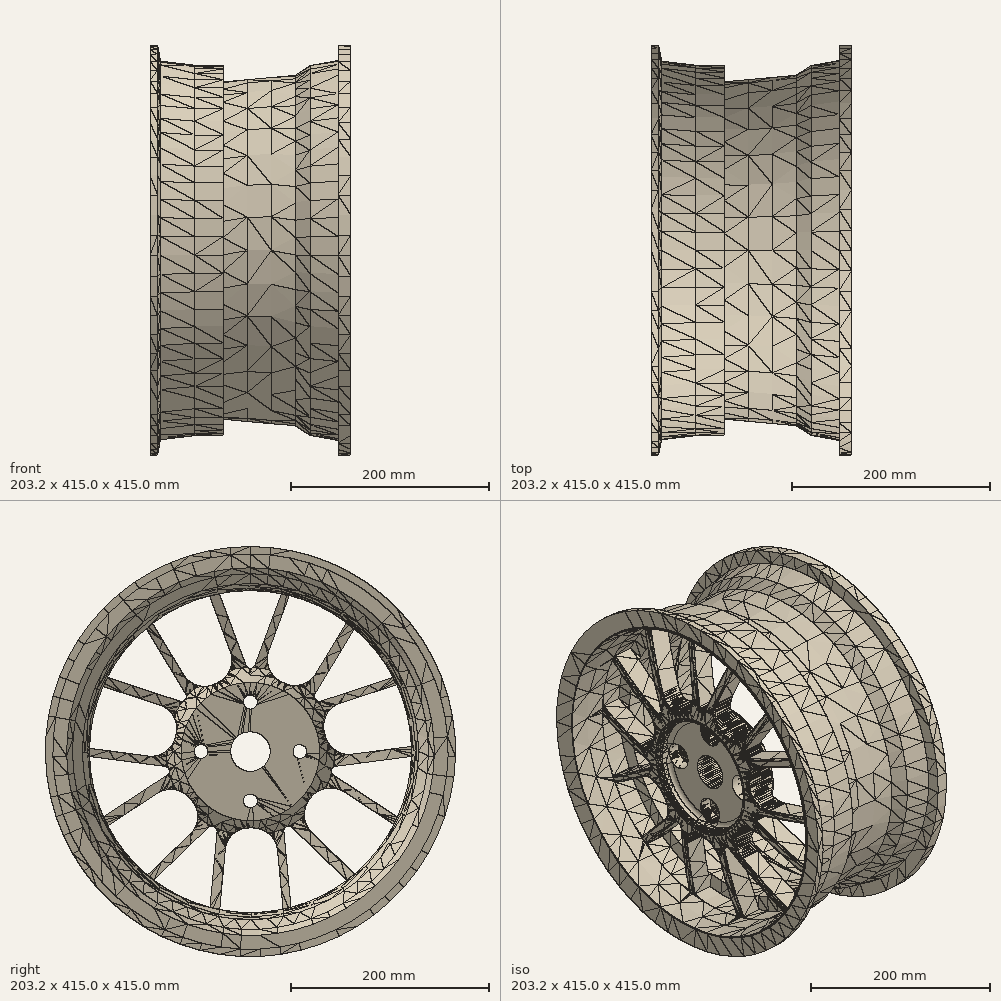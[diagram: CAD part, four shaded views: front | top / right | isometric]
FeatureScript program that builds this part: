
annotation { "Feature Type Name" : "Feature", "Feature Type Description" : "" }
export const myFeature = defineFeature(function(context is Context, id is Id, definition is map)
    precondition{}
    {
        {
            var Q0;
            Q0=qCreatedBy(makeId("Front.planeOp"),FACE);
            var sketch = newSketch(context, id + "F0", { "sketchPlane" : qUnion([Q0])});
            skLineSegment(sketch, "E0", {"start": v(0, 0) * mm, "end": v(203.2, 0) * mm});
            skLineSegment(sketch, "E1", {"start": v(203.2, 0) * mm, "end": v(203.2, 207.5) * mm});
            skPoint(sketch, "E2", {"position": v(203.2, 200) * mm});
            skLineSegment(sketch, "E3", {"start": v(203.2, 200) * mm, "end": v(197.7, 200) * mm});
            skPoint(sketch, "E4", {"position": v(197.7, 186) * mm});
            skLineSegment(sketch, "E5", {"start": v(197.7, 200) * mm, "end": v(197.7, 186) * mm});
            skPoint(sketch, "E6", {"position": v(164.7, 180) * mm});
            skLineSegment(sketch, "E7", {"start": v(164.7, 180) * mm, "end": v(197.7, 186) * mm});
            skPoint(sketch, "E8", {"position": v(149.7, 170) * mm});
            skLineSegment(sketch, "E9", {"start": v(164.7, 180) * mm, "end": v(149.7, 170) * mm});
            skPoint(sketch, "E10", {"position": v(66.7, 162.5) * mm});
            skLineSegment(sketch, "E11", {"start": v(66.7, 162.5) * mm, "end": v(149.7, 170) * mm});
            skLineSegment(sketch, "E12", {"start": v(203.2, 207.5) * mm, "end": v(66.7, 207.5) * mm});
            skLineSegment(sketch, "E13", {"start": v(0, 0) * mm, "end": v(0, 207.5) * mm});
            skPoint(sketch, "E14", {"position": v(2.5, 185) * mm});
            skPoint(sketch, "E15", {"position": v(45, 180) * mm});
            skLineSegment(sketch, "E16", {"start": v(45, 180) * mm, "end": v(66.7, 162.5) * mm});
            skLineSegment(sketch, "E17", {"start": v(2.5, 185) * mm, "end": v(45, 180) * mm});
            skLineSegment(sketch, "E18", {"start": v(0, 207.5) * mm, "end": v(66.7, 207.5) * mm});
            skLineSegment(sketch, "E19", {"start": v(2.5, 185) * mm, "end": v(0, 185) * mm});
            skLineSegment(sketch, "E20", {"start": v(2.5, 185) * mm, "end": v(2.5, 185.9) * mm});
            skLineSegment(sketch, "E21", {"start": v(3.1, 186.5) * mm, "end": v(3.4, 186.5) * mm});
            skLineSegment(sketch, "E22", {"start": v(0, 207.5) * mm, "end": v(4, 186.5) * mm});
            skPoint(sketch, "E23.visualSharp", {"position": v(2.5, 186.5) * mm});
            skArc(sketch, "E23.filletArc", {"start": v(3.1, 186.5) * mm, "mid": v(2.68, 186.32) * mm, "end": v(2.5, 185.9) * mm});
            skLineSegment(sketch, "E24", {"start": v(4, 185.9) * mm, "end": v(4, 185.5) * mm, "construction": true});
            skPoint(sketch, "E25.visualSharp", {"position": v(4, 186.5) * mm});
            skArc(sketch, "E25.filletArc", {"start": v(4, 185.9) * mm, "mid": v(3.82, 186.32) * mm, "end": v(3.4, 186.5) * mm});
            skLineSegment(sketch, "E26", {"start": v(4, 186.5) * mm, "end": v(4, 185.9) * mm});
            skLineSegment(sketch, "E27", {"start": v(66.7, 180) * mm, "end": v(45, 180) * mm});
            skLineSegment(sketch, "E28", {"start": v(66.7, 162.5) * mm, "end": v(66.7, 180) * mm});
            skArc(sketch, "E29", {"start": v(66.7, 162.5) * mm, "mid": v(58.94, 175.08) * mm, "end": v(45, 180) * mm});
            skLineSegment(sketch, "E30.0", {"start": v(203.2, 207.5) * mm, "end": v(190.2, 207.5) * mm});
            skLineSegment(sketch, "E30.1", {"start": v(66.03, 169.97) * mm, "end": v(66.7, 170.03) * mm});
            skLineSegment(sketch, "E30.2", {"start": v(161.83, 187.1) * mm, "end": v(147.13, 177.3) * mm});
            skLineSegment(sketch, "E30.3", {"start": v(161.83, 187.1) * mm, "end": v(190.2, 192.26) * mm});
            skLineSegment(sketch, "E30.4", {"start": v(190.2, 207.5) * mm, "end": v(190.2, 192.26) * mm});
            skLineSegment(sketch, "E31.0", {"start": v(10.67, 191.6) * mm, "end": v(45.44, 187.5) * mm});
            skLineSegment(sketch, "E31.1", {"start": v(7.63, 207.5) * mm, "end": v(10.67, 191.6) * mm});
            skLineSegment(sketch, "E32.0", {"start": v(74.2, 187.5) * mm, "end": v(45.44, 187.5) * mm});
            skLineSegment(sketch, "E32.1", {"start": v(74.2, 162.5) * mm, "end": v(74.2, 163.18) * mm});
            skLineSegment(sketch, "E33.trimOffspring", {"start": v(74.2, 170.7) * mm, "end": v(74.2, 187.5) * mm});
            skLineSegment(sketch, "E34.trimOffspring", {"start": v(74.2, 170.7) * mm, "end": v(147.13, 177.3) * mm});
            skPoint(sketch, "E35", {"position": v(45, -180) * mm});
            skPoint(sketch, "E36", {"position": v(16, 0) * mm});
            skArc(sketch, "E37", {"start": v(45, 180) * mm, "mid": v(23.3, 91.16) * mm, "end": v(16, 0) * mm});
            skArc(sketch, "E38.0", {"start": v(66.7, 162.54) * mm, "mid": v(48.21, 82.2) * mm, "end": v(42, 0) * mm});
            skLineSegment(sketch, "E39", {"start": v(16, 0) * mm, "end": v(42, 0) * mm});
            skLineSegment(sketch, "E40", {"start": v(16, 0) * mm, "end": v(16, 20) * mm});
            skLineSegment(sketch, "E41", {"start": v(16, 20) * mm, "end": v(76, 20) * mm});
            skPoint(sketch, "E42", {"position": v(66.2, 70) * mm});
            skPoint(sketch, "E43", {"position": v(48.64, 85) * mm});
            skLineSegment(sketch, "E44", {"start": v(66.2, 70) * mm, "end": v(48.64, 85) * mm});
            skLineSegment(sketch, "E45", {"start": v(66.2, 70) * mm, "end": v(66.2, 0) * mm});
            skSolve(sketch);
        }
        {
            var Q0;
            {var subQ3=sQuery(id+"F0.wireOp",EDGE,"E38.0");var subQ5=sQuery(id+"F0.wireOp",EDGE,"E41");var subQ7=makeQuery(id+"F0.imprint","INTERSECT",VERTEX,{"derivedFrom":[subQ3,subQ5]});Q0=makeQuery(id+"F0.imprint","IMPRINT",FACE,{"disambiguationData":[TD([[makeQuery(id+"F0.imprint","IMPRINT",EDGE,{"disambiguationData":[TD([[subQ7,1.0]])],"derivedFrom":subQ3}),-1.0]])]});}
            var Q1;
            {var subQ1=sQuery(id+"F0.wireOp",EDGE,"E16");var subQ3=sQuery(id+"F0.wireOp",EDGE,"E38.0");var subQ4=makeQuery(id+"F0.imprint","INTERSECT",VERTEX,{"derivedFrom":[subQ1,subQ3]});Q1=makeQuery(id+"F0.imprint","IMPRINT",FACE,{"disambiguationData":[TD([[makeQuery(id+"F0.imprint","IMPRINT",EDGE,{"disambiguationData":[TD([[subQ4,1.0]])],"derivedFrom":subQ3}),-1.0]])]});}
            var Q2;
            {var subQ1=sQuery(id+"F0.wireOp",EDGE,"E27");Q2=makeQuery(id+"F0.imprint","IMPRINT",FACE,{"disambiguationData":[TD([[makeQuery(id+"F0.imprint","IMPRINT",EDGE,{"derivedFrom":subQ1}),1.0]])]});}
            var Q3;
            {var subQ7=sQuery(id+"F0.wireOp",EDGE,"E3");Q3=makeQuery(id+"F0.imprint","IMPRINT",FACE,{"disambiguationData":[TD([[makeQuery(id+"F0.imprint","IMPRINT",EDGE,{"derivedFrom":subQ7}),-1.0]])]});}
            var Q4;
            {var subQ0=sQuery(id+"F0.wireOp",EDGE,"E44");Q4=makeQuery(id+"F0.imprint","IMPRINT",FACE,{"disambiguationData":[TD([[makeQuery(id+"F0.imprint","IMPRINT",EDGE,{"derivedFrom":subQ0}),1.0]])]});}
            var Q5;
            Q5=sQuery(id+"F0.wireOp",EDGE,"E0");
            revolve(context, id + "F1", {"entities" : qUnion([Q0, Q1, Q2, Q3, Q4]), "axis" : qUnion([Q5]), "revolveType" : RevolveType.FULL});
        }
        {
            var Q0;
            Q0=qCreatedBy(makeId("Right.planeOp"),FACE);
            cPlane(context, id + "F2", {"entities" : qUnion([Q0]), "cplaneType" : CPlaneType.OFFSET, "offset" : 16 * mm, "width" : 150 * mm, "height" : 150 * mm});
        }
        {
            var Q0;
            Q0=qCreatedBy(id+"F2.planeOp",FACE);
            var sketch = newSketch(context, id + "F3", { "sketchPlane" : qUnion([Q0])});
            skCircle(sketch, "E46.0", {"center": v(0, 0) * mm, "radius": 20 * mm});
            skCircle(sketch, "E47", {"center": v(0, 0) * mm, "radius": 50 * mm, "construction": true});
            skPoint(sketch, "E48", {"position": v(0, 50) * mm});
            skPoint(sketch, "E49", {"position": v(50, 0) * mm});
            skPoint(sketch, "E50", {"position": v(0, -50) * mm});
            skPoint(sketch, "E51", {"position": v(-50, 0) * mm});
            skCircle(sketch, "E52", {"center": v(0, 50) * mm, "radius": 7 * mm});
            skCircle(sketch, "E53", {"center": v(-50, 0) * mm, "radius": 7 * mm});
            skCircle(sketch, "E54", {"center": v(0, -50) * mm, "radius": 7 * mm});
            skCircle(sketch, "E55", {"center": v(50, 0) * mm, "radius": 7 * mm});
            skCircle(sketch, "E56", {"center": v(0, 0) * mm, "radius": 75 * mm});
            skPoint(sketch, "E57", {"position": v(0, 75) * mm});
            skCircle(sketch, "E58.0", {"center": v(0, 0) * mm, "radius": 180 * mm});
            skLineSegment(sketch, "E59", {"start": v(0, 75) * mm, "end": v(0, 180) * mm});
            skPoint(sketch, "E60.orphan", {"position": v(0, 193.6) * mm});
            skPoint(sketch, "E61", {"position": v(-37.5, 180) * mm});
            skLineSegment(sketch, "E62", {"start": v(-37.5, 180) * mm, "end": v(37.5, 180) * mm});
            skLineSegment(sketch, "E63", {"start": v(37.5, 180) * mm, "end": v(37.5, 176.05) * mm});
            skLineSegment(sketch, "E64", {"start": v(-37.5, 180) * mm, "end": v(-37.5, 176.05) * mm});
            skLineSegment(sketch, "E65", {"start": v(-37.5, 176.05) * mm, "end": v(-4.69, 87.63) * mm});
            skLineSegment(sketch, "E66", {"start": v(4.69, 87.63) * mm, "end": v(37.5, 176.05) * mm});
            skArc(sketch, "E67.filletArc", {"start": v(-4.69, 87.63) * mm, "mid": v(0, 84.37) * mm, "end": v(4.69, 87.63) * mm});
            skLineSegment(sketch, "E68.1.0", {"start": v(-65.6, 58.3) * mm, "end": v(-114.26, 139.08) * mm});
            skLineSegment(sketch, "E68.1.1", {"start": v(-161.02, 80.45) * mm, "end": v(-71.44, 50.97) * mm});
            skArc(sketch, "E68.1.2", {"start": v(-71.44, 50.97) * mm, "mid": v(-65.96, 52.6) * mm, "end": v(-65.6, 58.3) * mm});
            skLineSegment(sketch, "E68.2.0", {"start": v(-86.48, -14.93) * mm, "end": v(-179.98, -2.62) * mm});
            skLineSegment(sketch, "E68.2.1", {"start": v(-163.3, -75.73) * mm, "end": v(-84.4, -24.07) * mm});
            skArc(sketch, "E68.2.2", {"start": v(-84.4, -24.07) * mm, "mid": v(-82.26, -18.77) * mm, "end": v(-86.48, -14.93) * mm});
            skLineSegment(sketch, "E68.3.0", {"start": v(-42.25, -76.92) * mm, "end": v(-110.17, -142.35) * mm});
            skLineSegment(sketch, "E68.3.1", {"start": v(-42.6, -174.89) * mm, "end": v(-33.8, -80.99) * mm});
            skArc(sketch, "E68.3.2", {"start": v(-33.8, -80.99) * mm, "mid": v(-36.6, -76.02) * mm, "end": v(-42.25, -76.92) * mm});
            skLineSegment(sketch, "E68.4.0", {"start": v(33.8, -80.99) * mm, "end": v(42.6, -174.89) * mm});
            skLineSegment(sketch, "E68.4.1", {"start": v(110.17, -142.35) * mm, "end": v(42.25, -76.92) * mm});
            skArc(sketch, "E68.4.2", {"start": v(42.25, -76.92) * mm, "mid": v(36.6, -76.02) * mm, "end": v(33.8, -80.99) * mm});
            skLineSegment(sketch, "E68.5.0", {"start": v(84.4, -24.07) * mm, "end": v(163.3, -75.73) * mm});
            skLineSegment(sketch, "E68.5.1", {"start": v(179.98, -2.62) * mm, "end": v(86.48, -14.93) * mm});
            skArc(sketch, "E68.5.2", {"start": v(86.48, -14.93) * mm, "mid": v(82.26, -18.77) * mm, "end": v(84.4, -24.07) * mm});
            skLineSegment(sketch, "E68.6.0", {"start": v(71.44, 50.97) * mm, "end": v(161.02, 80.45) * mm});
            skLineSegment(sketch, "E68.6.1", {"start": v(114.26, 139.08) * mm, "end": v(65.6, 58.3) * mm});
            skArc(sketch, "E68.6.2", {"start": v(65.6, 58.3) * mm, "mid": v(65.96, 52.6) * mm, "end": v(71.44, 50.97) * mm});
            skPoint(sketch, "E69", {"position": v(45.5, 174.15) * mm});
            skLineSegment(sketch, "E70", {"start": v(45.5, 174.15) * mm, "end": v(18.69, 101.9) * mm});
            skPoint(sketch, "E71", {"position": v(106.26, 145.29) * mm});
            skLineSegment(sketch, "E72", {"start": v(106.26, 145.29) * mm, "end": v(66.32, 79) * mm});
            skLineSegment(sketch, "E73", {"start": v(34.22, 69.29) * mm, "end": v(31.44, 70.6) * mm});
            skPoint(sketch, "E74.visualSharp", {"position": v(10.7, 80.4) * mm});
            skArc(sketch, "E74.filletArc", {"start": v(18.69, 101.9) * mm, "mid": v(18.97, 83.77) * mm, "end": v(31.44, 70.6) * mm});
            skPoint(sketch, "E75.visualSharp", {"position": v(54.65, 59.63) * mm});
            skArc(sketch, "E75.filletArc", {"start": v(34.22, 69.29) * mm, "mid": v(52.14, 67.96) * mm, "end": v(66.32, 79) * mm});
            skLineSegment(sketch, "E76.1.0", {"start": v(-47.34, 173.66) * mm, "end": v(-20.4, 101.1) * mm});
            skLineSegment(sketch, "E76.1.1", {"start": v(-107.8, 144.16) * mm, "end": v(-68.02, 78.15) * mm});
            skArc(sketch, "E76.1.2", {"start": v(-68.02, 78.15) * mm, "mid": v(-53.66, 67.06) * mm, "end": v(-35.6, 68.6) * mm});
            skArc(sketch, "E76.1.3", {"start": v(-32.84, 69.96) * mm, "mid": v(-20.63, 83.14) * mm, "end": v(-20.4, 101.1) * mm});
            skLineSegment(sketch, "E76.1.4", {"start": v(-32.84, 69.96) * mm, "end": v(-35.6, 68.6) * mm});
            skLineSegment(sketch, "E76.2.0", {"start": v(-165.3, 71.27) * mm, "end": v(-91.77, 47.08) * mm});
            skLineSegment(sketch, "E76.2.1", {"start": v(-179.91, 5.6) * mm, "end": v(-103.5, -4.46) * mm});
            skArc(sketch, "E76.2.2", {"start": v(-103.5, -4.46) * mm, "mid": v(-85.9, -0.14) * mm, "end": v(-75.83, 14.94) * mm});
            skArc(sketch, "E76.2.3", {"start": v(-75.17, 17.95) * mm, "mid": v(-77.86, 35.7) * mm, "end": v(-91.77, 47.08) * mm});
            skLineSegment(sketch, "E76.2.4", {"start": v(-75.17, 17.95) * mm, "end": v(-75.83, 14.94) * mm});
            skLineSegment(sketch, "E76.3.0", {"start": v(-158.78, -84.8) * mm, "end": v(-94.02, -42.4) * mm});
            skLineSegment(sketch, "E76.3.1", {"start": v(-116.56, -137.17) * mm, "end": v(-61.05, -83.7) * mm});
            skArc(sketch, "E76.3.2", {"start": v(-61.05, -83.7) * mm, "mid": v(-53.44, -67.24) * mm, "end": v(-58.96, -49.97) * mm});
            skArc(sketch, "E76.3.3", {"start": v(-60.9, -47.58) * mm, "mid": v(-76.46, -38.61) * mm, "end": v(-94.02, -42.4) * mm});
            skLineSegment(sketch, "E76.3.4", {"start": v(-60.9, -47.58) * mm, "end": v(-58.96, -49.97) * mm});
            skLineSegment(sketch, "E76.4.0", {"start": v(-32.7, -177) * mm, "end": v(-25.48, -99.94) * mm});
            skLineSegment(sketch, "E76.4.1", {"start": v(34.57, -176.65) * mm, "end": v(27.38, -99.92) * mm});
            skArc(sketch, "E76.4.2", {"start": v(27.38, -99.92) * mm, "mid": v(19.25, -83.7) * mm, "end": v(2.3, -77.25) * mm});
            skArc(sketch, "E76.4.3", {"start": v(-0.77, -77.28) * mm, "mid": v(-17.49, -83.85) * mm, "end": v(-25.48, -99.94) * mm});
            skLineSegment(sketch, "E76.4.4", {"start": v(-0.77, -77.28) * mm, "end": v(2.3, -77.25) * mm});
            skLineSegment(sketch, "E76.5.0", {"start": v(118, -135.93) * mm, "end": v(62.25, -82.23) * mm});
            skLineSegment(sketch, "E76.5.1", {"start": v(159.66, -83.11) * mm, "end": v(95.2, -40.9) * mm});
            skArc(sketch, "E76.5.2", {"start": v(95.2, -40.9) * mm, "mid": v(77.45, -37.14) * mm, "end": v(61.84, -46.37) * mm});
            skArc(sketch, "E76.5.3", {"start": v(59.94, -48.78) * mm, "mid": v(54.66, -65.95) * mm, "end": v(62.25, -82.23) * mm});
            skLineSegment(sketch, "E76.5.4", {"start": v(59.94, -48.78) * mm, "end": v(61.84, -46.37) * mm});
            skLineSegment(sketch, "E76.6.0", {"start": v(179.84, 7.5) * mm, "end": v(103.1, -2.6) * mm});
            skLineSegment(sketch, "E76.6.1", {"start": v(164.53, 73.01) * mm, "end": v(91.32, 48.93) * mm});
            skArc(sketch, "E76.6.2", {"start": v(91.32, 48.93) * mm, "mid": v(77.32, 37.4) * mm, "end": v(74.8, 19.44) * mm});
            skArc(sketch, "E76.6.3", {"start": v(75.5, 16.45) * mm, "mid": v(85.64, 1.61) * mm, "end": v(103.1, -2.6) * mm});
            skLineSegment(sketch, "E76.6.4", {"start": v(75.5, 16.45) * mm, "end": v(74.8, 19.44) * mm});
            skSolve(sketch);
        }
        {
            var Q0;
            {var subQ0=sQuery(id+"F3.wireOp",EDGE,"E68.6.0");Q0=makeQuery(id+"F3.imprint","IMPRINT",FACE,{"disambiguationData":[TD([[makeQuery(id+"F3.imprint","IMPRINT",EDGE,{"derivedFrom":subQ0}),1.0]])]});}
            var Q1;
            {var subQ3=sQuery(id+"F3.wireOp",EDGE,"E66");Q1=makeQuery(id+"F3.imprint","IMPRINT",FACE,{"disambiguationData":[TD([[makeQuery(id+"F3.imprint","IMPRINT",EDGE,{"derivedFrom":subQ3}),1.0]])]});}
            var Q2;
            {var subQ3=sQuery(id+"F3.wireOp",EDGE,"E65");Q2=makeQuery(id+"F3.imprint","IMPRINT",FACE,{"disambiguationData":[TD([[makeQuery(id+"F3.imprint","IMPRINT",EDGE,{"derivedFrom":subQ3}),1.0]])]});}
            var Q3;
            {var subQ0=sQuery(id+"F3.wireOp",EDGE,"E68.1.0");Q3=makeQuery(id+"F3.imprint","IMPRINT",FACE,{"disambiguationData":[TD([[makeQuery(id+"F3.imprint","IMPRINT",EDGE,{"derivedFrom":subQ0}),1.0]])]});}
            var Q4;
            {var subQ0=sQuery(id+"F3.wireOp",EDGE,"E68.2.0");Q4=makeQuery(id+"F3.imprint","IMPRINT",FACE,{"disambiguationData":[TD([[makeQuery(id+"F3.imprint","IMPRINT",EDGE,{"derivedFrom":subQ0}),1.0]])]});}
            var Q5;
            {var subQ0=sQuery(id+"F3.wireOp",EDGE,"E68.3.0");Q5=makeQuery(id+"F3.imprint","IMPRINT",FACE,{"disambiguationData":[TD([[makeQuery(id+"F3.imprint","IMPRINT",EDGE,{"derivedFrom":subQ0}),1.0]])]});}
            var Q6;
            {var subQ0=sQuery(id+"F3.wireOp",EDGE,"E68.4.0");Q6=makeQuery(id+"F3.imprint","IMPRINT",FACE,{"disambiguationData":[TD([[makeQuery(id+"F3.imprint","IMPRINT",EDGE,{"derivedFrom":subQ0}),1.0]])]});}
            var Q7;
            {var subQ0=sQuery(id+"F3.wireOp",EDGE,"E68.5.0");Q7=makeQuery(id+"F3.imprint","IMPRINT",FACE,{"disambiguationData":[TD([[makeQuery(id+"F3.imprint","IMPRINT",EDGE,{"derivedFrom":subQ0}),1.0]])]});}
            var Q8;
            Q8=makeQuery(id+"F3.imprint","IMPRINT",FACE,{"disambiguationData":[TD([[makeQuery(id+"F3.imprint","IMPRINT",EDGE,{"derivedFrom":sQuery(id+"F3.wireOp",EDGE,"E52")}),1.0]])]});
            var Q9;
            Q9=makeQuery(id+"F3.imprint","IMPRINT",FACE,{"disambiguationData":[TD([[makeQuery(id+"F3.imprint","IMPRINT",EDGE,{"derivedFrom":sQuery(id+"F3.wireOp",EDGE,"E55")}),1.0]])]});
            var Q10;
            Q10=makeQuery(id+"F3.imprint","IMPRINT",FACE,{"disambiguationData":[TD([[makeQuery(id+"F3.imprint","IMPRINT",EDGE,{"derivedFrom":sQuery(id+"F3.wireOp",EDGE,"E54")}),1.0]])]});
            var Q11;
            Q11=makeQuery(id+"F3.imprint","IMPRINT",FACE,{"disambiguationData":[TD([[makeQuery(id+"F3.imprint","IMPRINT",EDGE,{"derivedFrom":sQuery(id+"F3.wireOp",EDGE,"E53")}),1.0]])]});
            var Q12;
            {var subQ1=sQuery(id+"F3.wireOp",EDGE,"E76.5.0");Q12=makeQuery(id+"F3.imprint","IMPRINT",FACE,{"disambiguationData":[TD([[makeQuery(id+"F3.imprint","IMPRINT",EDGE,{"derivedFrom":subQ1}),-1.0]])]});}
            var Q13;
            {var subQ1=sQuery(id+"F3.wireOp",EDGE,"E76.6.0");Q13=makeQuery(id+"F3.imprint","IMPRINT",FACE,{"disambiguationData":[TD([[makeQuery(id+"F3.imprint","IMPRINT",EDGE,{"derivedFrom":subQ1}),-1.0]])]});}
            var Q14;
            {var subQ1=sQuery(id+"F3.wireOp",EDGE,"E76.4.0");Q14=makeQuery(id+"F3.imprint","IMPRINT",FACE,{"disambiguationData":[TD([[makeQuery(id+"F3.imprint","IMPRINT",EDGE,{"derivedFrom":subQ1}),-1.0]])]});}
            var Q15;
            {var subQ1=sQuery(id+"F3.wireOp",EDGE,"E76.3.0");Q15=makeQuery(id+"F3.imprint","IMPRINT",FACE,{"disambiguationData":[TD([[makeQuery(id+"F3.imprint","IMPRINT",EDGE,{"derivedFrom":subQ1}),-1.0]])]});}
            var Q16;
            {var subQ0=sQuery(id+"F3.wireOp",EDGE,"E76.2.0");Q16=makeQuery(id+"F3.imprint","IMPRINT",FACE,{"disambiguationData":[TD([[makeQuery(id+"F3.imprint","IMPRINT",EDGE,{"derivedFrom":subQ0}),-1.0]])]});}
            var Q17;
            {var subQ1=sQuery(id+"F3.wireOp",EDGE,"E76.1.0");Q17=makeQuery(id+"F3.imprint","IMPRINT",FACE,{"disambiguationData":[TD([[makeQuery(id+"F3.imprint","IMPRINT",EDGE,{"derivedFrom":subQ1}),-1.0]])]});}
            var Q18;
            {var subQ1=sQuery(id+"F3.wireOp",EDGE,"E70");Q18=makeQuery(id+"F3.imprint","IMPRINT",FACE,{"disambiguationData":[TD([[makeQuery(id+"F3.imprint","IMPRINT",EDGE,{"derivedFrom":subQ1}),1.0]])]});}
            extrude(context, id + "F4", {"entities" : qUnion([Q0, Q1, Q2, Q3, Q4, Q5, Q6, Q7, Q8, Q9, Q10, Q11, Q12, Q13, Q14, Q15, Q16, Q17, Q18]), "operationType" : NewBodyOperationType.REMOVE, "depth" : 55 * mm});
        }
        {
            var Q0;
            Q0=qCreatedBy(id+"F2.planeOp",FACE);
            var sketch = newSketch(context, id + "F5", { "sketchPlane" : qUnion([Q0])});
            skCircle(sketch, "E77.0", {"center": v(0, 0) * mm, "radius": 20 * mm});
            skCircle(sketch, "E78", {"center": v(0, 0) * mm, "radius": 65 * mm});
            skCircle(sketch, "E79.0", {"center": v(0, 50) * mm, "radius": 7 * mm, "construction": true});
            skCircle(sketch, "E80.0", {"center": v(50, 0) * mm, "radius": 7 * mm, "construction": true});
            skCircle(sketch, "E81.0", {"center": v(-50, 0) * mm, "radius": 7 * mm, "construction": true});
            skCircle(sketch, "E82.0", {"center": v(0, -50) * mm, "radius": 7 * mm, "construction": true});
            skCircle(sketch, "E83", {"center": v(0, 50) * mm, "radius": 15 * mm});
            skCircle(sketch, "E84", {"center": v(-50, 0) * mm, "radius": 15 * mm});
            skCircle(sketch, "E85", {"center": v(0, -50) * mm, "radius": 15 * mm});
            skCircle(sketch, "E86", {"center": v(50, 0) * mm, "radius": 15 * mm});
            skSolve(sketch);
        }
        {
            var Q0;
            Q0=qSketchRegion(id+"F5",true);
            var Q1;
            {var subQ0=sQuery(id+"F5.wireOp",EDGE,"E83");var subQ1=sQuery(id+"F5.wireOp",EDGE,"E77.0");var subQ2=makeQuery(id+"F5.imprint","INTERSECT",VERTEX,{"disambiguationData":[OD(0.0)],"derivedFrom":[subQ1,subQ0]});Q1=makeQuery(id+"F5.imprint","IMPRINT",FACE,{"disambiguationData":[TD([[makeQuery(id+"F5.imprint","IMPRINT",EDGE,{"disambiguationData":[TD([[subQ2,-1.0]])],"derivedFrom":subQ1}),-1.0]])]});}
            var Q2;
            {var subQ0=sQuery(id+"F5.wireOp",EDGE,"E85");var subQ1=sQuery(id+"F5.wireOp",EDGE,"E77.0");var subQ2=makeQuery(id+"F5.imprint","INTERSECT",VERTEX,{"disambiguationData":[OD(0.0)],"derivedFrom":[subQ1,subQ0]});Q2=makeQuery(id+"F5.imprint","IMPRINT",FACE,{"disambiguationData":[TD([[makeQuery(id+"F5.imprint","IMPRINT",EDGE,{"disambiguationData":[TD([[subQ2,-1.0]])],"derivedFrom":subQ1}),-1.0]])]});}
            var Q3;
            {var subQ0=sQuery(id+"F5.wireOp",EDGE,"E84");var subQ1=sQuery(id+"F5.wireOp",EDGE,"E77.0");var subQ2=makeQuery(id+"F5.imprint","INTERSECT",VERTEX,{"disambiguationData":[OD(0.0)],"derivedFrom":[subQ1,subQ0]});Q3=makeQuery(id+"F5.imprint","IMPRINT",FACE,{"disambiguationData":[TD([[makeQuery(id+"F5.imprint","IMPRINT",EDGE,{"disambiguationData":[TD([[subQ2,-1.0]])],"derivedFrom":subQ1}),-1.0]])]});}
            var Q4;
            {var subQ0=sQuery(id+"F5.wireOp",EDGE,"E86");var subQ1=sQuery(id+"F5.wireOp",EDGE,"E77.0");var subQ2=makeQuery(id+"F5.imprint","INTERSECT",VERTEX,{"disambiguationData":[OD(0.0)],"derivedFrom":[subQ1,subQ0]});Q4=makeQuery(id+"F5.imprint","IMPRINT",FACE,{"disambiguationData":[TD([[makeQuery(id+"F5.imprint","IMPRINT",EDGE,{"disambiguationData":[TD([[subQ2,1.0]])],"derivedFrom":subQ1}),-1.0]])]});}
            var Q5;
            Q5=makeQuery(id+"F5.imprint","IMPRINT",FACE,{"disambiguationData":[TD([[makeQuery(id+"F5.imprint","IMPRINT",EDGE,{"derivedFrom":sQuery(id+"F5.wireOp",EDGE,"E86")}),1.0]])]});
            var Q6;
            Q6=makeQuery(id+"F5.imprint","IMPRINT",FACE,{"disambiguationData":[TD([[makeQuery(id+"F5.imprint","IMPRINT",EDGE,{"derivedFrom":sQuery(id+"F5.wireOp",EDGE,"E83")}),1.0]])]});
            var Q7;
            Q7=makeQuery(id+"F5.imprint","IMPRINT",FACE,{"disambiguationData":[TD([[makeQuery(id+"F5.imprint","IMPRINT",EDGE,{"derivedFrom":sQuery(id+"F5.wireOp",EDGE,"E84")}),1.0]])]});
            var Q8;
            Q8=makeQuery(id+"F5.imprint","IMPRINT",FACE,{"disambiguationData":[TD([[makeQuery(id+"F5.imprint","IMPRINT",EDGE,{"derivedFrom":sQuery(id+"F5.wireOp",EDGE,"E85")}),1.0]])]});
            extrude(context, id + "F6", {"entities" : qUnion([Q0, Q1, Q2, Q3, Q4, Q5, Q6, Q7, Q8]), "operationType" : NewBodyOperationType.REMOVE, "depth" : 20 * mm});
        }
        {
            var Q0;
            Q0=makeQuery(id+"F6.boolean.opBoolean","COPY",FACE,{"derivedFrom":makeQuery(id+"F6.opExtrude","CAP_FACE",FACE,{"disambiguationData":[OSD([sQuery(id+"F5.wireOp",EDGE,"E77.0"),sQuery(id+"F5.wireOp",EDGE,"E78")])],"isStart":false})});
            var sketch = newSketch(context, id + "F7", { "sketchPlane" : qUnion([Q0])});
            skCircle(sketch, "E87.0", {"center": v(0, 50) * mm, "radius": 7 * mm, "construction": true});
            skCircle(sketch, "E88", {"center": v(0, 50) * mm, "radius": 15 * mm});
            skCircle(sketch, "E89.1.0", {"center": v(-50, 0) * mm, "radius": 15 * mm});
            skCircle(sketch, "E89.2.0", {"center": v(0, -50) * mm, "radius": 15 * mm});
            skCircle(sketch, "E89.3.0", {"center": v(50, 0) * mm, "radius": 15 * mm});
            skPoint(sketch, "E89.center", {"position": v(0, 0) * mm});
            skSolve(sketch);
        }
        {
            var Q0;
            Q0=qSketchRegion(id+"F7",true);
            extrude(context, id + "F8", {"entities" : qUnion([Q0]), "operationType" : NewBodyOperationType.REMOVE, "oppositeDirection" : true, "depth" : 15 * mm});
        }
        {
            var Q0;
            Q0=makeQuery(id+"F6.boolean.opBoolean","INTERSECT",EDGE,{"derivedFrom":[makeQuery(id+"F1.opRevolve","SWEPT_FACE",FACE,{"disambiguationData":[OSD([sQuery(id+"F0.wireOp",EDGE,"E37")])]}),makeQuery(id+"F6.opExtrude","SWEPT_FACE",FACE,{"disambiguationData":[OSD([sQuery(id+"F5.wireOp",EDGE,"E78")])]})]});
            var Q1;
            {var subQ0=sQuery(id+"F5.wireOp",EDGE,"E78");Q1=makeQuery(id+"F8.boolean.opBoolean","SPLIT",EDGE,{"disambiguationData":[TD([makeQuery(id+"F6.boolean.opBoolean","COPY",FACE,{"derivedFrom":makeQuery(id+"F6.opExtrude","CAP_FACE",FACE,{"disambiguationData":[OSD([sQuery(id+"F5.wireOp",EDGE,"E77.0"),subQ0])],"isStart":false})}),makeQuery(id+"F6.boolean.opBoolean","COPY",FACE,{"derivedFrom":makeQuery(id+"F6.opExtrude","SWEPT_FACE",FACE,{"disambiguationData":[OSD([subQ0])]})}),makeQuery(id+"F8.opExtrude","SWEPT_FACE",FACE,{"disambiguationData":[OSD([sQuery(id+"F7.wireOp",EDGE,"E88")])]}),makeQuery(id+"F8.opExtrude","SWEPT_FACE",FACE,{"disambiguationData":[OSD([sQuery(id+"F7.wireOp",EDGE,"E89.1.0")])]})])],"derivedFrom":makeQuery(id+"F6.boolean.opBoolean","COPY",EDGE,{"derivedFrom":makeQuery(id+"F6.opExtrude","CAP_EDGE",EDGE,{"disambiguationData":[OSD([subQ0])],"isStart":false})})});}
            fillet(context, id + "F9", {"entities" : qUnion([Q0, Q1]), "radius" : 5 * mm, "tangentPropagation" : true, "allowEdgeOverflow" : false});
        }
        {
            var Q0;
            Q0=makeQuery(id+"F4.boolean.opBoolean","INTERSECT",EDGE,{"derivedFrom":[makeQuery(id+"F1.opRevolve","SWEPT_FACE",FACE,{"disambiguationData":[OSD([sQuery(id+"F0.wireOp",EDGE,"E37")])]}),makeQuery(id+"F4.opExtrude","SWEPT_FACE",FACE,{"disambiguationData":[OSD([sQuery(id+"F3.wireOp",EDGE,"E76.6.0")])]})]});
            var Q1;
            Q1=makeQuery(id+"F4.boolean.opBoolean","INTERSECT",EDGE,{"derivedFrom":[makeQuery(id+"F1.opRevolve","SWEPT_FACE",FACE,{"disambiguationData":[OSD([sQuery(id+"F0.wireOp",EDGE,"E37")])]}),makeQuery(id+"F4.opExtrude","SWEPT_FACE",FACE,{"disambiguationData":[OSD([sQuery(id+"F3.wireOp",EDGE,"E68.5.1")])]})]});
            var Q2;
            Q2=makeQuery(id+"F4.boolean.opBoolean","INTERSECT",EDGE,{"derivedFrom":[makeQuery(id+"F1.opRevolve","SWEPT_FACE",FACE,{"disambiguationData":[OSD([sQuery(id+"F0.wireOp",EDGE,"E37")])]}),makeQuery(id+"F4.opExtrude","SWEPT_FACE",FACE,{"disambiguationData":[OSD([sQuery(id+"F3.wireOp",EDGE,"E76.5.1")])]})]});
            var Q3;
            Q3=makeQuery(id+"F4.boolean.opBoolean","INTERSECT",EDGE,{"derivedFrom":[makeQuery(id+"F1.opRevolve","SWEPT_FACE",FACE,{"disambiguationData":[OSD([sQuery(id+"F0.wireOp",EDGE,"E37")])]}),makeQuery(id+"F4.opExtrude","SWEPT_FACE",FACE,{"disambiguationData":[OSD([sQuery(id+"F3.wireOp",EDGE,"E68.4.1")])]})]});
            var Q4;
            Q4=makeQuery(id+"F4.boolean.opBoolean","INTERSECT",EDGE,{"derivedFrom":[makeQuery(id+"F1.opRevolve","SWEPT_FACE",FACE,{"disambiguationData":[OSD([sQuery(id+"F0.wireOp",EDGE,"E37")])]}),makeQuery(id+"F4.opExtrude","SWEPT_FACE",FACE,{"disambiguationData":[OSD([sQuery(id+"F3.wireOp",EDGE,"E76.4.1")])]})]});
            var Q5;
            Q5=makeQuery(id+"F4.boolean.opBoolean","INTERSECT",EDGE,{"derivedFrom":[makeQuery(id+"F1.opRevolve","SWEPT_FACE",FACE,{"disambiguationData":[OSD([sQuery(id+"F0.wireOp",EDGE,"E37")])]}),makeQuery(id+"F4.opExtrude","SWEPT_FACE",FACE,{"disambiguationData":[OSD([sQuery(id+"F3.wireOp",EDGE,"E68.3.1")])]})]});
            var Q6;
            Q6=makeQuery(id+"F4.boolean.opBoolean","INTERSECT",EDGE,{"derivedFrom":[makeQuery(id+"F1.opRevolve","SWEPT_FACE",FACE,{"disambiguationData":[OSD([sQuery(id+"F0.wireOp",EDGE,"E37")])]}),makeQuery(id+"F4.opExtrude","SWEPT_FACE",FACE,{"disambiguationData":[OSD([sQuery(id+"F3.wireOp",EDGE,"E76.3.1")])]})]});
            var Q7;
            Q7=makeQuery(id+"F4.boolean.opBoolean","INTERSECT",EDGE,{"derivedFrom":[makeQuery(id+"F1.opRevolve","SWEPT_FACE",FACE,{"disambiguationData":[OSD([sQuery(id+"F0.wireOp",EDGE,"E37")])]}),makeQuery(id+"F4.opExtrude","SWEPT_FACE",FACE,{"disambiguationData":[OSD([sQuery(id+"F3.wireOp",EDGE,"E68.2.1")])]})]});
            var Q8;
            Q8=makeQuery(id+"F4.boolean.opBoolean","INTERSECT",EDGE,{"derivedFrom":[makeQuery(id+"F1.opRevolve","SWEPT_FACE",FACE,{"disambiguationData":[OSD([sQuery(id+"F0.wireOp",EDGE,"E37")])]}),makeQuery(id+"F4.opExtrude","SWEPT_FACE",FACE,{"disambiguationData":[OSD([sQuery(id+"F3.wireOp",EDGE,"E76.2.1")])]})]});
            var Q9;
            Q9=makeQuery(id+"F4.boolean.opBoolean","INTERSECT",EDGE,{"derivedFrom":[makeQuery(id+"F1.opRevolve","SWEPT_FACE",FACE,{"disambiguationData":[OSD([sQuery(id+"F0.wireOp",EDGE,"E37")])]}),makeQuery(id+"F4.opExtrude","SWEPT_FACE",FACE,{"disambiguationData":[OSD([sQuery(id+"F3.wireOp",EDGE,"E68.1.1")])]})]});
            var Q10;
            Q10=makeQuery(id+"F4.boolean.opBoolean","INTERSECT",EDGE,{"derivedFrom":[makeQuery(id+"F1.opRevolve","SWEPT_FACE",FACE,{"disambiguationData":[OSD([sQuery(id+"F0.wireOp",EDGE,"E37")])]}),makeQuery(id+"F4.opExtrude","SWEPT_FACE",FACE,{"disambiguationData":[OSD([sQuery(id+"F3.wireOp",EDGE,"E76.1.1")])]})]});
            var Q11;
            Q11=makeQuery(id+"F4.boolean.opBoolean","INTERSECT",EDGE,{"derivedFrom":[makeQuery(id+"F1.opRevolve","SWEPT_FACE",FACE,{"disambiguationData":[OSD([sQuery(id+"F0.wireOp",EDGE,"E37")])]}),makeQuery(id+"F4.opExtrude","SWEPT_FACE",FACE,{"disambiguationData":[OSD([sQuery(id+"F3.wireOp",EDGE,"E65")])]})]});
            var Q12;
            Q12=makeQuery(id+"F4.boolean.opBoolean","INTERSECT",EDGE,{"derivedFrom":[makeQuery(id+"F1.opRevolve","SWEPT_FACE",FACE,{"disambiguationData":[OSD([sQuery(id+"F0.wireOp",EDGE,"E37")])]}),makeQuery(id+"F4.opExtrude","SWEPT_FACE",FACE,{"disambiguationData":[OSD([sQuery(id+"F3.wireOp",EDGE,"E70")])]})]});
            var Q13;
            Q13=makeQuery(id+"F4.boolean.opBoolean","INTERSECT",EDGE,{"derivedFrom":[makeQuery(id+"F1.opRevolve","SWEPT_FACE",FACE,{"disambiguationData":[OSD([sQuery(id+"F0.wireOp",EDGE,"E37")])]}),makeQuery(id+"F4.opExtrude","SWEPT_FACE",FACE,{"disambiguationData":[OSD([sQuery(id+"F3.wireOp",EDGE,"E68.6.1")])]})]});
            fillet(context, id + "F10", {"entities" : qUnion([Q0, Q1, Q2, Q3, Q4, Q5, Q6, Q7, Q8, Q9, Q10, Q11, Q12, Q13]), "radius" : 2 * mm, "tangentPropagation" : true, "allowEdgeOverflow" : false});
        }
    });
